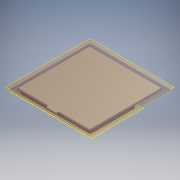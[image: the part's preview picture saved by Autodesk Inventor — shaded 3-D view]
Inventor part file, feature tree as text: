
AUTODESK INVENTOR PART (.ipt)
format: ipt  version: 2017 (Build 210142000, 142)  size: 429,568 bytes
history: native  units: mm
features: move_body x15, direct_edit x12, reference x11, sketch x7, extrude x6, other x5, plane x3, fillet x3, chamfer x1
ambient origin geometry x8: Origin, YZ Plane, XZ Plane, XY Plane, X Axis, Y Axis, Z Axis, Center Point
bodies: Solid1 (feature_tree)
feature tree (63):
  plane  "Work Plane1"
  extrude  "Extrusion1"  Depth=2.0mm
  sketch  "Sketch2"  dims[d3=5.5mm d4=2.0mm]
  plane  "Work Plane2"
  plane  "Work Plane3"
  extrude  "Extrusion2"  Depth=2.0mm
  extrude  "Extrusion3"  Depth=1.0mm
  extrude  "Extrusion4"  Depth=1.5mm TaperAngle=0.0deg
  extrude  "Extrusion5"  Depth=1.0mm TaperAngle=0.0deg
  fillet  "Fillet1"  Radius=1.75mm
  direct_edit  "Direct Edit1"
  fillet  "Fillet2"  Radius=1.0mm
  direct_edit  "Direct Edit2"
  direct_edit  "Direct Edit3"
  direct_edit  "Direct Edit4"
  direct_edit  "Direct Edit5"
  direct_edit  "Direct Edit6"
  direct_edit  "Direct Edit7"
  direct_edit  "Direct Edit8"
  direct_edit  "Direct Edit9"
  direct_edit  "Direct Edit10"
  chamfer  "Chamfer2"  Distance=15.5mm
  direct_edit  "Direct Edit11"
  sketch  "Sketch6"  dims[d23=2.0mm d24=0.0mm d25=0.0mm d26=15.5mm]
  direct_edit  "Direct Edit12"
  extrude  "Extrusion6"  Depth=0.5mm TaperAngle=0.0deg
  fillet  "Fillet3"  [1 undecoded]
  sketch  "Sketch1"  dims[d0=2.0mm d1=0.0mm d2=5.5mm]
  reference  "Reference2"
  sketch  "Sketch3"  dims[d5=1.0mm d6=0.0mm d7=1.0mm]
  reference  "Reference3"
  reference  "Reference4"
  reference  "Reference5"
  reference  "Reference6"
  reference  "Reference7"
  reference  "Reference8"
  reference  "Reference9"
  reference  "Reference10"
  reference  "Reference11"
  reference  "Reference12"
  sketch  "Sketch4"  dims[d8=100.0mm d10=7.62mm d11=10.0mm d13=10.0mm d15=1.5mm d16=0.0mm]
  sketch  "Sketch5"  dims[d17=1.5mm d18=3.75mm d19=0.0mm d20=1.75mm d21=0.0mm d22=1.0mm]
  sketch  "Sketch7"  dims[d27=0.0mm d28=0.0mm d29=-5.5mm d30=0.0mm d31=0.0mm d32=0.5mm d33=0.0mm d34=0.0mm d35=-4.0mm d36=0.0mm d37=0.0mm d38=2.5mm d39=0.0mm d40=0.0mm d41=-0.5mm d42=0.0mm d43=0.0mm d44=0.5mm d45=0.0mm d46=0.0mm d47=-0.5mm d48=0.0mm d49=0.0mm d50=-0.5mm d51=0.0mm d52=0.0mm d53=-0.5mm d57=0.0mm d58=0.0mm d59=-0.5mm d60=0.0mm d61=0.0mm d62=-0.9mm d63=0.0mm d64=0.0mm d65=-0.5mm d66=0.5mm d67=1.0mm d68=45.0deg d69=0.0mm d70=0.0mm d71=-13.0mm d72=0.0mm d73=0.0mm d74=0.6mm d75=13.0mm d76=6.0mm d77=1.5mm d78=0.0mm d79=2.0mm]
  parser-record x2  (decoder bookkeeping rows leaked as tree rows — omitted from the tree; the rows remain in map.json)
  other  "protoswitchboard.iam"
  other  "cover:1"
  other  "Delete1"
  move_body  "Move1"
  move_body  "Move2"
  move_body  "Move3"
  move_body  "Move4"
  move_body  "Move5"
  move_body  "Move6"
  move_body  "Move7"
  move_body  "Move8"
  move_body  "Move9"
  move_body  "Move10"
  move_body  "Move11"
  move_body  "Move12"
  move_body  "Move13"
  move_body  "Move14"
  move_body  "Move15"
note: 1 required parameter value undecoded (feature->parameter linkage not recoverable at this tier; creation-order binding heuristic only, values carry confidence <= 0.55)
note: 2 file-system paths scrubbed to <path> (originals preserved in map.json)
